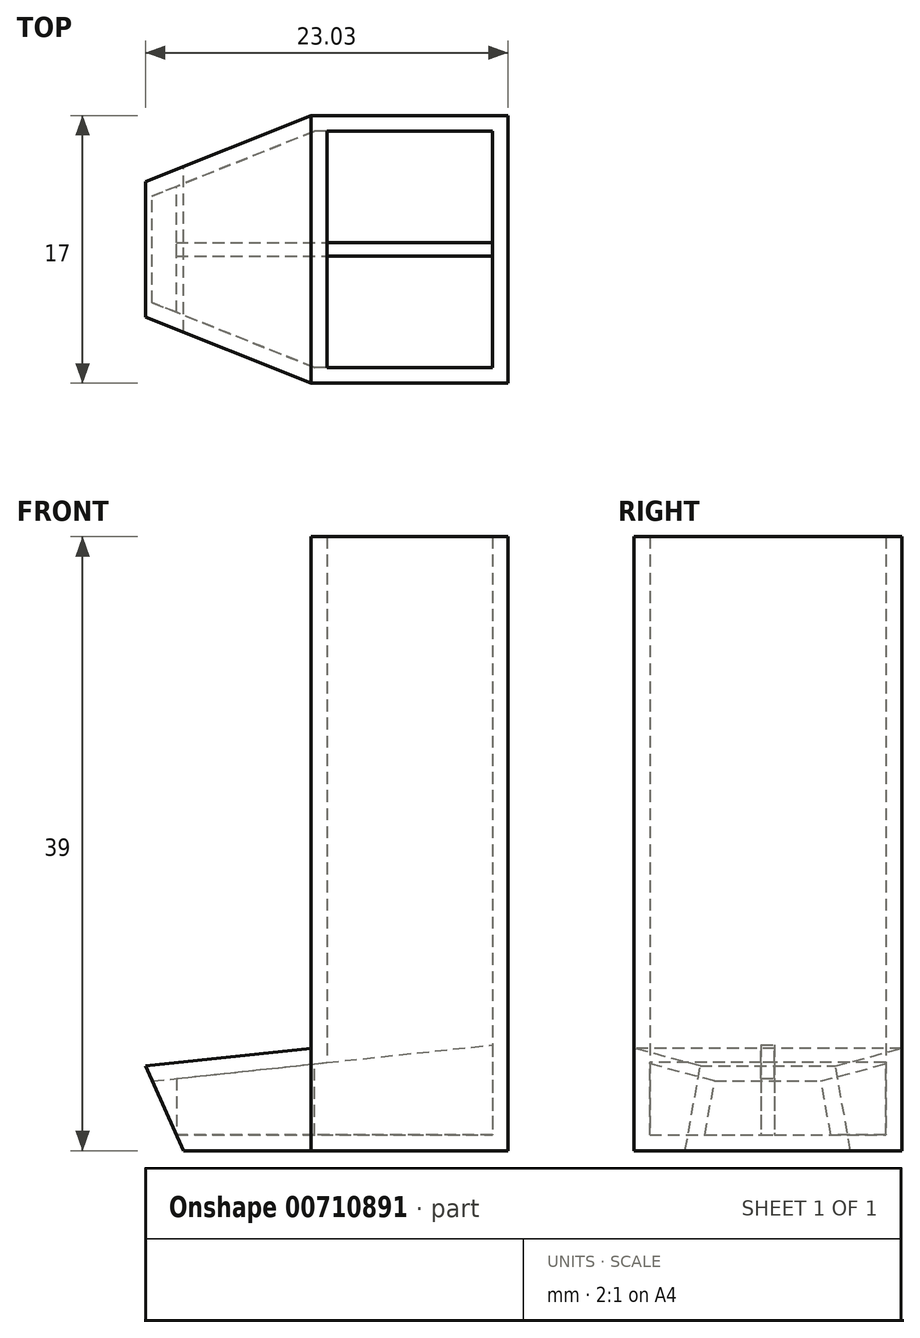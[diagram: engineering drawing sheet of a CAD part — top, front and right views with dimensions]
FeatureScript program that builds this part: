
annotation { "Feature Type Name" : "Feature", "Feature Type Description" : "" }
export const myFeature = defineFeature(function(context is Context, id is Id, definition is map)
    precondition{}
    {
        {
            var Q0;
            Q0=qCreatedBy(makeId("Top.planeOp"),FACE);
            var sketch = newSketch(context, id + "F0", { "sketchPlane" : qUnion([Q0])});
            skLineSegment(sketch, "E0.bottom", {"start": v(6.25, -8.5) * mm, "end": v(-6.25, -8.5) * mm});
            skLineSegment(sketch, "E0.top", {"start": v(6.25, 8.5) * mm, "end": v(-6.25, 8.5) * mm});
            skLineSegment(sketch, "E0.left", {"start": v(6.25, -8.5) * mm, "end": v(6.25, 8.5) * mm});
            skLineSegment(sketch, "E0.right", {"start": v(-6.25, -8.5) * mm, "end": v(-6.25, 8.5) * mm});
            skPoint(sketch, "E0.middle", {"position": v(0, 0) * mm});
            skSolve(sketch);
        }
        {
            var Q0;
            Q0 = qSketchRegion(id + "F0", true);
            extrude(context, id + "F1", {"entities" : qUnion([Q0]), "depth" : 36 * mm, "offsetDistance" : 25 * mm});
        }
        {
            var Q0;
            Q0=makeQuery(id+"F1.opExtrude","SWEPT_FACE",FACE,{"disambiguationData":[OSD([sQuery(id+"F0.wireOp",EDGE,"E0.right")])]});
            var sketch = newSketch(context, id + "F2", { "sketchPlane" : qUnion([Q0])});
            skLineSegment(sketch, "E1.bottom", {"start": v(-8.5, 0) * mm, "end": v(8.5, 0) * mm});
            skLineSegment(sketch, "E1.top", {"start": v(-8.5, 5) * mm, "end": v(8.5, 5) * mm});
            skLineSegment(sketch, "E1.left", {"start": v(-8.5, 0) * mm, "end": v(-8.5, 5) * mm});
            skLineSegment(sketch, "E1.right", {"start": v(8.5, 0) * mm, "end": v(8.5, 5) * mm});
            skSolve(sketch);
        }
        {
            var Q0;
            Q0 = qSketchRegion(id + "F2", true);
            extrude(context, id + "F3", {"entities" : qUnion([Q0]), "operationType" : NewBodyOperationType.ADD, "depth" : 15 * mm, "offsetDistance" : 25 * mm});
        }
        {
            var Q0;
            Q0=makeQuery(id+"F3.opExtrude","SWEPT_FACE",FACE,{"disambiguationData":[OSD([sQuery(id+"F2.wireOp",EDGE,"E1.top")])]});
            var sketch = newSketch(context, id + "F4", { "sketchPlane" : qUnion([Q0])});
            skLineSegment(sketch, "E2", {"start": v(-6.25, 8.5) * mm, "end": v(-21.25, 2.5) * mm});
            skLineSegment(sketch, "E3", {"start": v(-6.25, -8.5) * mm, "end": v(-21.25, -2.5) * mm});
            skSolve(sketch);
        }
        {
            var Q0;
            {var subQ0=sQuery(id+"F4.wireOp",EDGE,"E3");Q0=makeQuery(id+"F4.imprint","IMPRINT",FACE,{"disambiguationData":[TD([[makeQuery(id+"F4.imprint","IMPRINT",EDGE,{"derivedFrom":subQ0}),1.0]])]});}
            var Q1;
            {var subQ0=sQuery(id+"F4.wireOp",EDGE,"E2");Q1=makeQuery(id+"F4.imprint","IMPRINT",FACE,{"disambiguationData":[TD([[makeQuery(id+"F4.imprint","IMPRINT",EDGE,{"derivedFrom":subQ0}),-1.0]])]});}
            extrude(context, id + "F5", {"entities" : qUnion([Q0, Q1]), "operationType" : NewBodyOperationType.REMOVE, "oppositeDirection" : true, "depth" : 25 * mm, "offsetDistance" : 25 * mm});
        }
        {
            var Q0;
            Q0=makeQuery(id+"F3.opExtrude","SWEPT_FACE",FACE,{"disambiguationData":[OSD([sQuery(id+"F2.wireOp",EDGE,"E1.top")])]});
            extrude(context, id + "F6", {"entities" : qUnion([Q0]), "operationType" : NewBodyOperationType.ADD, "depth" : 1.5 * mm, "offsetDistance" : 25 * mm});
        }
        {
            var Q0;
            Q0=makeQuery(id+"F6.opExtrude","CAP_FACE",FACE,{"disambiguationData":[OSD([sQuery(id+"F2.wireOp",EDGE,"E1.top")])],"isStart":false});
            var sketch = newSketch(context, id + "F7", { "sketchPlane" : qUnion([Q0])});
            skLineSegment(sketch, "E4", {"start": v(-17.8, 3.88) * mm, "end": v(-17.8, -3.88) * mm});
            skSolve(sketch);
        }
        {
            var Q0;
            {var subQ0=sQuery(id+"F7.wireOp",EDGE,"E4");Q0=makeQuery(id+"F7.imprint","IMPRINT",FACE,{"disambiguationData":[TD([[makeQuery(id+"F7.imprint","IMPRINT",EDGE,{"derivedFrom":subQ0}),-1.0]])]});}
            extrude(context, id + "F8", {"entities" : qUnion([Q0]), "operationType" : NewBodyOperationType.REMOVE, "oppositeDirection" : true, "depth" : 25 * mm, "offsetDistance" : 25 * mm});
        }
        {
            var Q0;
            Q0=makeQuery(id+"F1.opExtrude","CAP_FACE",FACE,{"disambiguationData":[OSD([sQuery(id+"F0.wireOp",EDGE,"E0.bottom"),sQuery(id+"F0.wireOp",EDGE,"E0.top"),sQuery(id+"F0.wireOp",EDGE,"E0.left"),sQuery(id+"F0.wireOp",EDGE,"E0.right")])],"isStart":false});
            extrude(context, id + "F9", {"entities" : qUnion([Q0]), "operationType" : NewBodyOperationType.ADD, "depth" : 3 * mm, "offsetDistance" : 25 * mm});
        }
        {
            var Q0;
            {var subQ0=sQuery(id+"F0.wireOp",EDGE,"E0.top");Q0=makeQuery(id+"F9.boolean.opBoolean","MERGE",FACE,{"derivedFrom":[makeQuery(id+"F3.boolean.opBoolean","MERGE",FACE,{"derivedFrom":[makeQuery(id+"F1.opExtrude","SWEPT_FACE",FACE,{"disambiguationData":[OSD([subQ0])]}),makeQuery(id+"F3.opExtrude","SWEPT_FACE",FACE,{"disambiguationData":[OSD([sQuery(id+"F2.wireOp",EDGE,"E1.left")])]})]}),makeQuery(id+"F9.opExtrude","SWEPT_FACE",FACE,{"disambiguationData":[OSD([subQ0]),TDD([makeQuery(id+"F1.opExtrude","CAP_EDGE",EDGE,{"disambiguationData":[OSD([subQ0])],"isStart":false})])]})]});}
            var sketch = newSketch(context, id + "F10", { "sketchPlane" : qUnion([Q0])});
            skLineSegment(sketch, "E5", {"start": v(14.36, 0) * mm, "end": v(18.35, 8.89) * mm});
            skLineSegment(sketch, "E6", {"start": v(18.35, 8.89) * mm, "end": v(22.22, 10.1) * mm});
            skLineSegment(sketch, "E7", {"start": v(22.22, 10.1) * mm, "end": v(28.06, -5.33) * mm});
            skLineSegment(sketch, "E8", {"start": v(28.06, -5.33) * mm, "end": v(14.36, 0) * mm});
            skLineSegment(sketch, "E9", {"start": v(16.78, 5.38) * mm, "end": v(6.25, 6.5) * mm});
            skLineSegment(sketch, "E10", {"start": v(6.25, 6.5) * mm, "end": v(12.75, 11.89) * mm});
            skLineSegment(sketch, "E11", {"start": v(12.75, 11.89) * mm, "end": v(22.22, 10.1) * mm});
            skSolve(sketch);
        }
        {
            var Q0;
            Q0 = qSketchRegion(id + "F10", true);
            extrude(context, id + "F11", {"entities" : qUnion([Q0]), "operationType" : NewBodyOperationType.REMOVE, "oppositeDirection" : true, "depth" : 25 * mm, "offsetDistance" : 25 * mm});
        }
        {
            var Q0;
            Q0=makeQuery(id+"F9.opExtrude","CAP_FACE",FACE,{"disambiguationData":[OSD([sQuery(id+"F0.wireOp",EDGE,"E0.bottom"),sQuery(id+"F0.wireOp",EDGE,"E0.top"),sQuery(id+"F0.wireOp",EDGE,"E0.left"),sQuery(id+"F0.wireOp",EDGE,"E0.right")])],"isStart":false});
            var Q1;
            Q1=makeQuery(id+"F11.boolean.opBoolean","COPY",FACE,{"derivedFrom":makeQuery(id+"F11.opExtrude","SWEPT_FACE",FACE,{"disambiguationData":[OSD([sQuery(id+"F10.wireOp",EDGE,"E5")])]})});
            shell(context, id + "F12", {"entities" : qUnion([Q0, Q1]), "thickness" : 1 * mm});
        }
        {
            var Q0;
            Q0=makeQuery(id+"F12.opShell","OFFSET_FACE",FACE,{"disambiguationData":[OSD([sQuery(id+"F0.wireOp",EDGE,"E0.bottom"),sQuery(id+"F0.wireOp",EDGE,"E0.top"),sQuery(id+"F0.wireOp",EDGE,"E0.left"),sQuery(id+"F0.wireOp",EDGE,"E0.right"),sQuery(id+"F2.wireOp",EDGE,"E1.bottom")])]});
            var sketch = newSketch(context, id + "F13", { "sketchPlane" : qUnion([Q0])});
            skLineSegment(sketch, "E12.bottom", {"start": v(-27.45, -0.43) * mm, "end": v(11.9, -0.43) * mm});
            skLineSegment(sketch, "E12.top", {"start": v(-27.45, 0.43) * mm, "end": v(11.9, 0.43) * mm});
            skLineSegment(sketch, "E12.left", {"start": v(-27.45, -0.43) * mm, "end": v(-27.45, 0.43) * mm});
            skLineSegment(sketch, "E12.right", {"start": v(11.9, -0.43) * mm, "end": v(11.9, 0.43) * mm});
            skPoint(sketch, "E12.middle", {"position": v(-7.77, 0) * mm});
            skSolve(sketch);
        }
        {
            var Q0;
            {var subQ0=sQuery(id+"F13.wireOp",EDGE,"E12.bottom");var subQ3=sQuery(id+"F0.wireOp",EDGE,"E0.left");var subQ4=makeQuery(id+"F12.opShell","OFFSET_EDGE",EDGE,{"disambiguationData":[OSD([subQ3]),TDD([makeQuery(id+"F1.opExtrude","CAP_EDGE",EDGE,{"disambiguationData":[OSD([subQ3])],"isStart":true})])]});var subQ5=makeQuery(id+"F13.imprint","INTERSECT",VERTEX,{"derivedFrom":[subQ4,subQ0]});Q0=makeQuery(id+"F13.imprint","IMPRINT",FACE,{"disambiguationData":[TD([[makeQuery(id+"F13.imprint","IMPRINT",EDGE,{"disambiguationData":[TD([[subQ5,-1.0]])],"derivedFrom":subQ4}),1.0]])]});}
            var Q1;
            Q1=makeQuery(id+"F12.opShell","OFFSET_FACE",FACE,{"disambiguationData":[OSD([sQuery(id+"F10.wireOp",EDGE,"E9")])]});
            extrude(context, id + "F14", {"entities" : qUnion([Q0]), "operationType" : NewBodyOperationType.ADD, "endBound" : BoundingType.UP_TO_SURFACE, "depth" : 10 * mm, "endBoundEntityFace" : qUnion([Q1]), "offsetDistance" : 25 * mm});
        }
    });
